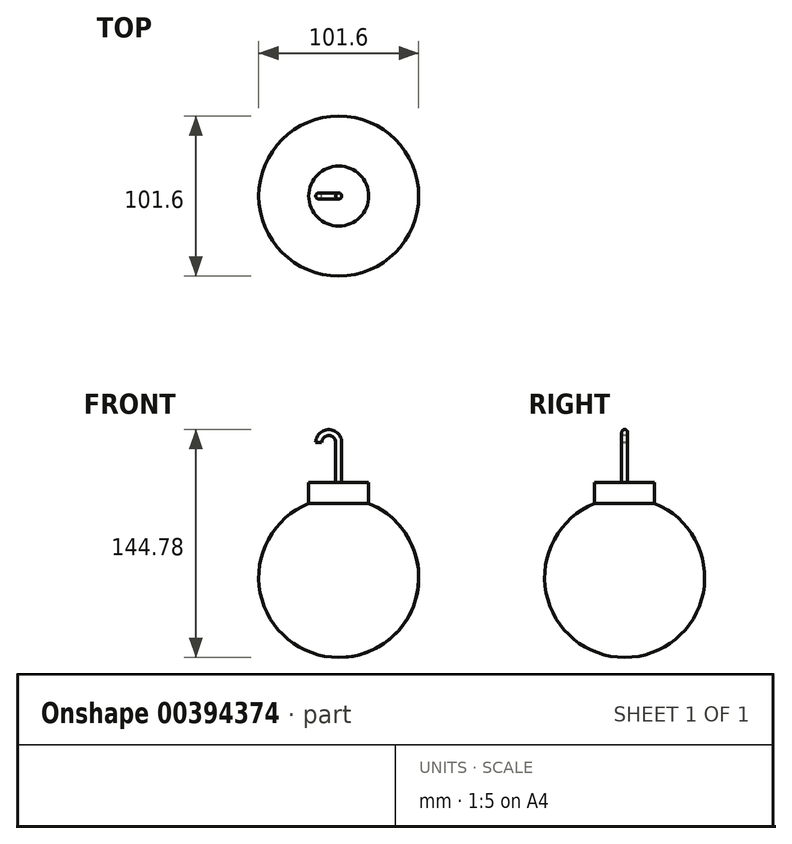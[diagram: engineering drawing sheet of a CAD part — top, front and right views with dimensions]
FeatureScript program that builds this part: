
annotation { "Feature Type Name" : "Feature", "Feature Type Description" : "" }
export const myFeature = defineFeature(function(context is Context, id is Id, definition is map)
    precondition{}
    {
        {
            var Q0;
            Q0=qCreatedBy(makeId("Top.planeOp"),FACE);
            var sketch = newSketch(context, id + "F0", { "sketchPlane" : qUnion([Q0])});
            skCircle(sketch, "E0", {"center": v(0, 0) * mm, "radius": 50.8 * mm});
            skLineSegment(sketch, "E1", {"start": v(0, 0) * mm, "end": v(-50.8, 0) * mm});
            skSolve(sketch);
        }
        {
            var Q0;
            Q0=qCreatedBy(makeId("Front.planeOp"),FACE);
            var sketch = newSketch(context, id + "F1", { "sketchPlane" : qUnion([Q0])});
            skLineSegment(sketch, "E2", {"start": v(0, 0) * mm, "end": v(0, 50.8) * mm});
            skArc(sketch, "E3", {"start": v(0, 50.8) * mm, "mid": v(-35.92, 35.92) * mm, "end": v(-50.8, 0) * mm});
            skLineSegment(sketch, "E4", {"start": v(-50.8, 0) * mm, "end": v(0, 0) * mm});
            skLineSegment(sketch, "E5", {"start": v(0, 0) * mm, "end": v(0, -50.8) * mm});
            skArc(sketch, "E6", {"start": v(-50.8, 0) * mm, "mid": v(-35.92, -35.92) * mm, "end": v(0, -50.8) * mm});
            skSolve(sketch);
        }
        {
            var Q0;
            Q0=makeQuery(id+"F1.imprint","IMPRINT",FACE,{"disambiguationData":[TD([[makeQuery(id+"F1.imprint","IMPRINT",EDGE,{"derivedFrom":sQuery(id+"F1.wireOp",EDGE,"E2")}),1.0]])]});
            var Q1;
            Q1=makeQuery(id+"F1.imprint","IMPRINT",FACE,{"disambiguationData":[TD([[makeQuery(id+"F1.imprint","IMPRINT",EDGE,{"derivedFrom":sQuery(id+"F1.wireOp",EDGE,"E4")}),-1.0]])]});
            var Q2;
            Q2=sQuery(id+"F1.wireOp",EDGE,"E2");
            revolve(context, id + "F2", {"entities" : qUnion([Q0, Q1]), "axis" : qUnion([Q2]), "revolveType" : RevolveType.FULL});
        }
        {
            var Q0;
            Q0=qCreatedBy(makeId("Top.planeOp"),FACE);
            cPlane(context, id + "F3", {"entities" : qUnion([Q0]), "cplaneType" : CPlaneType.OFFSET, "offset" : 50.8 * mm, "width" : 152.4 * mm, "height" : 152.4 * mm});
        }
        {
            var Q0;
            Q0=qCreatedBy(id+"F3.planeOp",FACE);
            var sketch = newSketch(context, id + "F4", { "sketchPlane" : qUnion([Q0])});
            skCircle(sketch, "E7", {"center": v(0, 0) * mm, "radius": 19.05 * mm});
            skSolve(sketch);
        }
        {
            var Q0;
            Q0 = qSketchRegion(id + "F4", true);
            extrude(context, id + "F5", {"entities" : qUnion([Q0]), "operationType" : NewBodyOperationType.ADD, "endBound" : BoundingType.SYMMETRIC, "depth" : 19.05 * mm});
        }
        {
            var Q0;
            Q0=makeQuery(id+"F5.opExtrude","CAP_FACE",FACE,{"disambiguationData":[OSD([sQuery(id+"F4.wireOp",EDGE,"E7")])],"isStart":false});
            var sketch = newSketch(context, id + "F6", { "sketchPlane" : qUnion([Q0])});
            skCircle(sketch, "E8", {"center": v(0, 0) * mm, "radius": 1.9 * mm});
            skSolve(sketch);
        }
        {
            var Q0;
            Q0 = qSketchRegion(id + "F6", true);
            extrude(context, id + "F7", {"entities" : qUnion([Q0]), "operationType" : NewBodyOperationType.ADD, "depth" : 25.4 * mm});
        }
        {
            var Q0;
            Q0=makeQuery(id+"F7.opExtrude","CAP_FACE",FACE,{"disambiguationData":[OSD([sQuery(id+"F6.wireOp",EDGE,"E8")])],"isStart":false});
            var sketch = newSketch(context, id + "F8", { "sketchPlane" : qUnion([Q0])});
            skLineSegment(sketch, "E9", {"start": v(-6.35, 0) * mm, "end": v(-6.35, -2.54) * mm});
            skLineSegment(sketch, "E10", {"start": v(-6.35, 0) * mm, "end": v(-6.35, 2.54) * mm});
            skSolve(sketch);
        }
        {
            var Q0;
            Q0=makeQuery(id+"F8.imprint","IMPRINT",FACE,{"disambiguationData":[TD([[makeQuery(id+"F8.imprint","IMPRINT",EDGE,{"derivedFrom":makeQuery(id+"F7.opExtrude","CAP_EDGE",EDGE,{"disambiguationData":[OSD([sQuery(id+"F6.wireOp",EDGE,"E8")])],"isStart":false})}),1.0]])]});
            var Q1;
            Q1=sQuery(id+"F8.wireOp",EDGE,"E9");
            revolve(context, id + "F9", {"operationType" : NewBodyOperationType.ADD, "entities" : qUnion([Q0]), "axis" : qUnion([Q1]), "revolveType" : RevolveType.ONE_DIRECTION, "angle" : 180 * degree});
        }
    });
